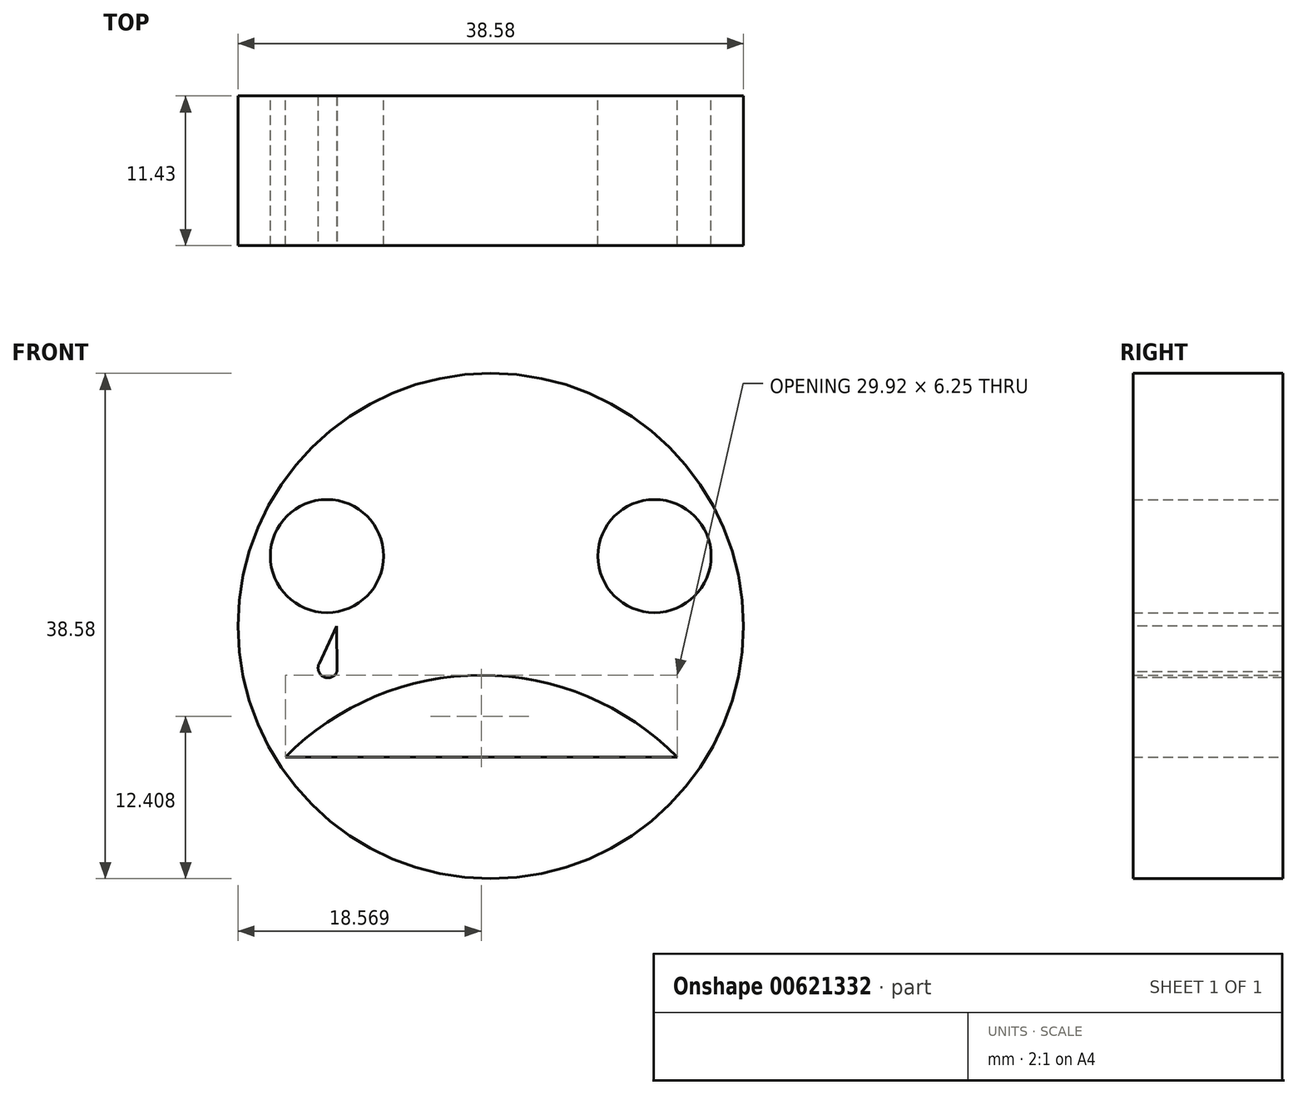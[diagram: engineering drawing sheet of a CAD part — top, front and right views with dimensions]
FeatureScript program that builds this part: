
annotation { "Feature Type Name" : "Feature", "Feature Type Description" : "" }
export const myFeature = defineFeature(function(context is Context, id is Id, definition is map)
    precondition{}
    {
        {
            var Q0;
            Q0=qCreatedBy(makeId("Front.planeOp"),FACE);
            var sketch = newSketch(context, id + "F0", { "sketchPlane" : qUnion([Q0])});
            skCircle(sketch, "E0", {"center": v(0, 0) * mm, "radius": 19.3 * mm});
            skLineSegment(sketch, "E1", {"start": v(-16.35, -10.57) * mm, "end": v(-16.14, -10.57) * mm});
            skArc(sketch, "E2", {"start": v(15, -10.57) * mm, "mid": v(-0.68, -3.49) * mm, "end": v(-16.35, -10.57) * mm});
            skCircle(sketch, "E3", {"center": v(-12.5, 5.34) * mm, "radius": 4.32 * mm});
            skCircle(sketch, "E4.MirrorC", {"center": v(12.5, 5.34) * mm, "radius": 4.32 * mm});
            skSolve(sketch);
        }
        {
            var Q0;
            Q0=makeQuery(id+"F0.imprint","IMPRINT",FACE,{"disambiguationData":[TD([[makeQuery(id+"F0.imprint","IMPRINT",EDGE,{"derivedFrom":sQuery(id+"F0.wireOp",EDGE,"E3")}),-1.0]])]});
            extrude(context, id + "F1", {"entities" : qUnion([Q0]), "depth" : 11.43 * mm, "offsetDistance" : 25.4 * mm});
        }
        {
            var Q0;
            Q0=qCreatedBy(makeId("Front.planeOp"),FACE);
            var sketch = newSketch(context, id + "F2", { "sketchPlane" : qUnion([Q0])});
            skArc(sketch, "E5", {"start": v(14.24, -10) * mm, "mid": v(-0.72, -3.76) * mm, "end": v(-15.68, -10) * mm});
            skLineSegment(sketch, "E6", {"start": v(-15.68, -10) * mm, "end": v(14.24, -10) * mm});
            skSolve(sketch);
        }
        {
            var Q0;
            Q0=sQuery(id+"F2.wireOp",EDGE,"E5");
            extrude(context, id + "F3", {"bodyType" : ToolBodyType.SURFACE, "surfaceEntities" : qUnion([Q0]), "depth" : 11.43 * mm, "offsetDistance" : 25.4 * mm});
        }
        {
            var Q0;
            Q0=makeQuery(id+"F2.imprint","IMPRINT",FACE,{"disambiguationData":[TD([[makeQuery(id+"F2.imprint","IMPRINT",EDGE,{"derivedFrom":sQuery(id+"F2.wireOp",EDGE,"E5")}),1.0]])]});
            extrude(context, id + "F4", {"entities" : qUnion([Q0]), "operationType" : NewBodyOperationType.REMOVE, "depth" : 25.4 * mm, "offsetDistance" : 25.4 * mm});
        }
        {
            var Q0;
            Q0=makeQuery(id+"F1.opExtrude","CAP_FACE",FACE,{"disambiguationData":[OSD([sQuery(id+"F0.wireOp",EDGE,"E0"),sQuery(id+"F0.wireOp",EDGE,"E3"),sQuery(id+"F0.wireOp",EDGE,"E4.MirrorC")])],"isStart":false});
            var sketch = newSketch(context, id + "F5", { "sketchPlane" : qUnion([Q0])});
            skLineSegment(sketch, "E7", {"start": v(-11.78, 0) * mm, "end": v(-13.1, -2.9) * mm});
            skArc(sketch, "E8", {"start": v(-13.1, -2.9) * mm, "mid": v(-12.73, -3.9) * mm, "end": v(-11.74, -3.5) * mm});
            skLineSegment(sketch, "E9", {"start": v(-11.78, 0) * mm, "end": v(-11.74, -3.5) * mm});
            skSolve(sketch);
        }
        {
            var Q0;
            Q0=makeQuery(id+"F5.imprint","IMPRINT",FACE,{"disambiguationData":[TD([[makeQuery(id+"F5.imprint","IMPRINT",EDGE,{"derivedFrom":sQuery(id+"F5.wireOp",EDGE,"E7")}),1.0]])]});
            extrude(context, id + "F6", {"entities" : qUnion([Q0]), "operationType" : NewBodyOperationType.REMOVE, "oppositeDirection" : true, "depth" : 25.4 * mm, "offsetDistance" : 25.4 * mm});
        }
    });
